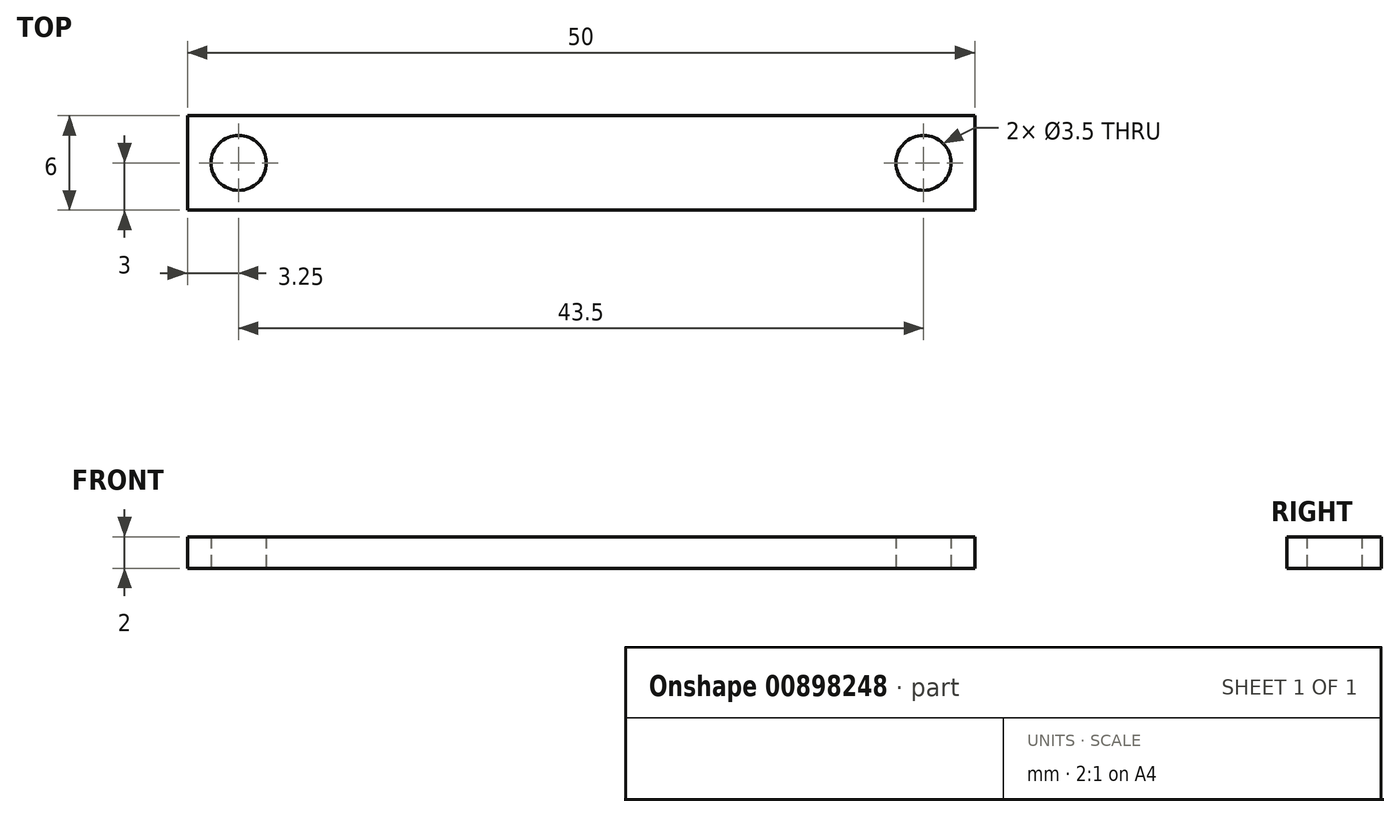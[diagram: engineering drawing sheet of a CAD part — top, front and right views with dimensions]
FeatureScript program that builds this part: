
annotation { "Feature Type Name" : "Feature", "Feature Type Description" : "" }
export const myFeature = defineFeature(function(context is Context, id is Id, definition is map)
    precondition{}
    {
        {
            var Q0;
            Q0=qCreatedBy(makeId("Top.planeOp"),FACE);
            var sketch = newSketch(context, id + "F0", { "sketchPlane" : qUnion([Q0])});
            skLineSegment(sketch, "E0.bottom", {"start": v(0, 0) * mm, "end": v(50, 0) * mm});
            skLineSegment(sketch, "E0.top", {"start": v(0, 6) * mm, "end": v(50, 6) * mm});
            skLineSegment(sketch, "E0.left", {"start": v(0, 0) * mm, "end": v(0, 6) * mm});
            skLineSegment(sketch, "E0.right", {"start": v(50, 0) * mm, "end": v(50, 6) * mm});
            skCircle(sketch, "E1", {"center": v(3.25, 3) * mm, "radius": 1.75 * mm});
            skCircle(sketch, "E2", {"center": v(46.75, 3) * mm, "radius": 1.75 * mm});
            skSolve(sketch);
        }
        {
            var Q0;
            Q0 = qSketchRegion(id + "F0", true);
            extrude(context, id + "F1", {"entities" : qUnion([Q0]), "depth" : 2 * mm, "offsetDistance" : 25 * mm});
        }
    });
